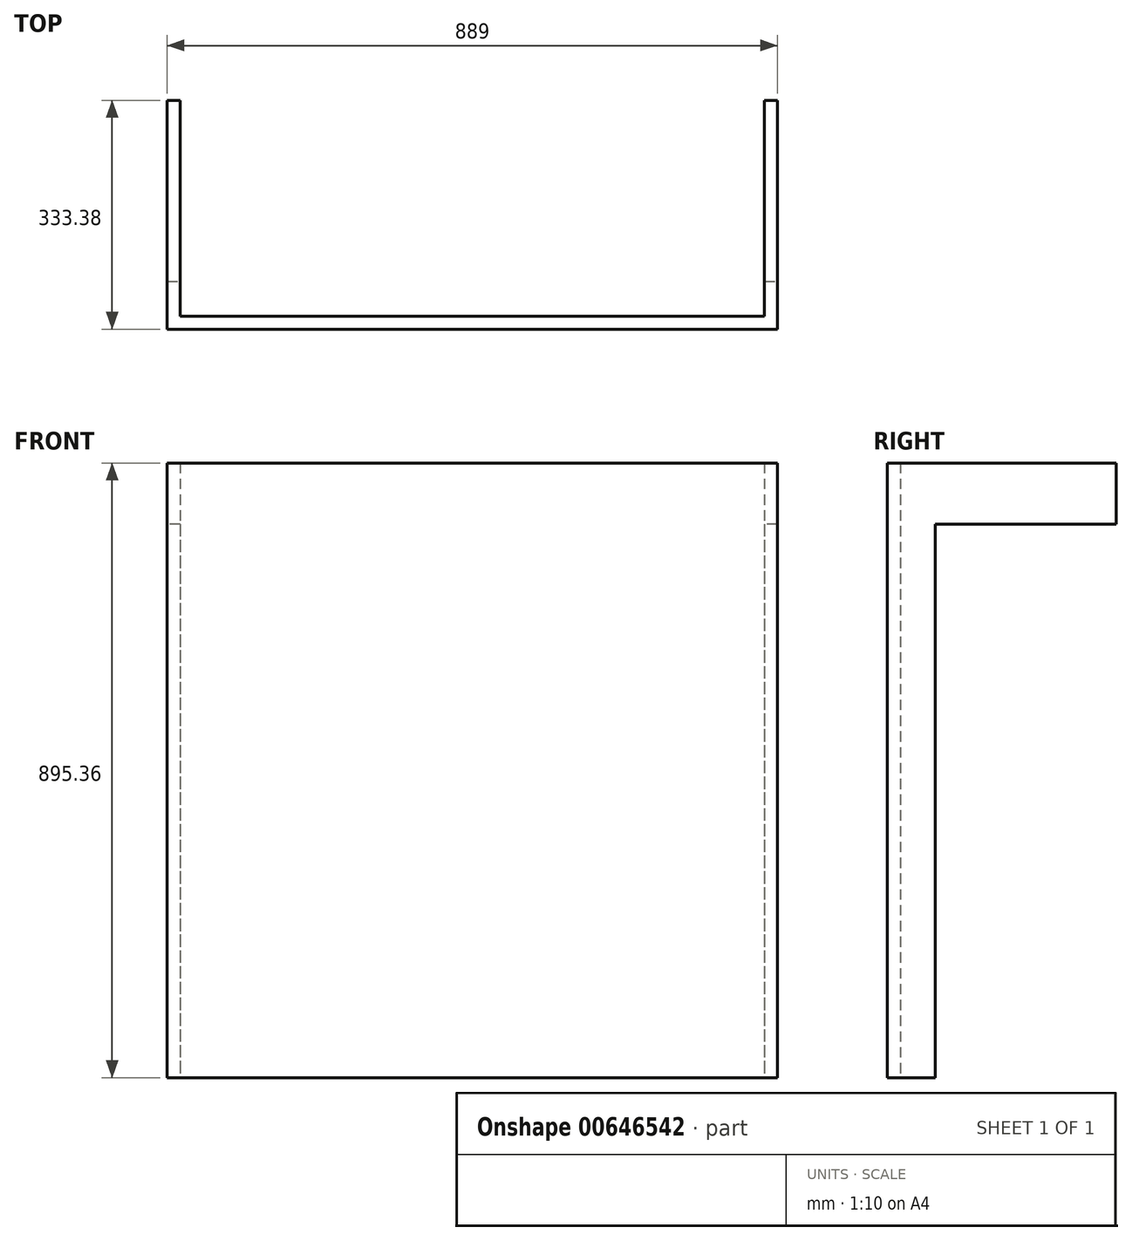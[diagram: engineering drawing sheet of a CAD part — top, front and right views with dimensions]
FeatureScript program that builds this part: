
annotation { "Feature Type Name" : "Feature", "Feature Type Description" : "" }
export const myFeature = defineFeature(function(context is Context, id is Id, definition is map)
    precondition{}
    {
        {
            var Q0;
            Q0=qCreatedBy(makeId("Front.planeOp"),FACE);
            var sketch = newSketch(context, id + "F0", { "sketchPlane" : qUnion([Q0])});
            skLineSegment(sketch, "E0.bottom", {"start": v(-444.5, 447.68) * mm, "end": v(444.5, 447.68) * mm});
            skLineSegment(sketch, "E0.top", {"start": v(-444.5, -447.68) * mm, "end": v(444.5, -447.68) * mm});
            skLineSegment(sketch, "E0.left", {"start": v(-444.5, 447.68) * mm, "end": v(-444.5, -447.68) * mm});
            skLineSegment(sketch, "E0.right", {"start": v(444.5, 447.68) * mm, "end": v(444.5, -447.68) * mm});
            skPoint(sketch, "E0.middle", {"position": v(0, 0) * mm});
            skSolve(sketch);
        }
        {
            var Q0;
            Q0=makeQuery(id+"F0.imprint","IMPRINT",FACE,{"disambiguationData":[TD([[makeQuery(id+"F0.imprint","IMPRINT",EDGE,{"derivedFrom":sQuery(id+"F0.wireOp",EDGE,"E0.bottom")}),-1.0]])]});
            extrude(context, id + "F1", {"entities" : qUnion([Q0]), "depth" : 19.05 * mm, "offsetDistance" : 25.4 * mm});
        }
        {
            var Q0;
            Q0=makeQuery(id+"F1.opExtrude","CAP_FACE",FACE,{"disambiguationData":[OSD([sQuery(id+"F0.wireOp",EDGE,"E0.bottom"),sQuery(id+"F0.wireOp",EDGE,"E0.top"),sQuery(id+"F0.wireOp",EDGE,"E0.left"),sQuery(id+"F0.wireOp",EDGE,"E0.right")])],"isStart":true});
            var sketch = newSketch(context, id + "F2", { "sketchPlane" : qUnion([Q0])});
            skLineSegment(sketch, "E1.bottom", {"start": v(-444.5, 447.68) * mm, "end": v(-425.45, 447.68) * mm});
            skLineSegment(sketch, "E1.top", {"start": v(-444.5, -447.68) * mm, "end": v(-425.45, -447.68) * mm});
            skLineSegment(sketch, "E1.left", {"start": v(-444.5, 447.68) * mm, "end": v(-444.5, -447.68) * mm});
            skLineSegment(sketch, "E1.right", {"start": v(-425.45, 447.68) * mm, "end": v(-425.45, -447.68) * mm});
            skLineSegment(sketch, "E2.bottom", {"start": v(444.5, 447.68) * mm, "end": v(425.45, 447.68) * mm});
            skLineSegment(sketch, "E2.top", {"start": v(444.5, -447.68) * mm, "end": v(425.45, -447.68) * mm});
            skLineSegment(sketch, "E2.left", {"start": v(444.5, 447.68) * mm, "end": v(444.5, -447.68) * mm});
            skLineSegment(sketch, "E2.right", {"start": v(425.45, 447.68) * mm, "end": v(425.45, -447.68) * mm});
            skSolve(sketch);
        }
        {
            var Q0;
            Q0=makeQuery(id+"F2.imprint","IMPRINT",FACE,{"disambiguationData":[TD([[makeQuery(id+"F2.imprint","IMPRINT",EDGE,{"derivedFrom":sQuery(id+"F2.wireOp",EDGE,"E1.bottom")}),1.0]])]});
            var Q1;
            Q1=makeQuery(id+"F2.imprint","IMPRINT",FACE,{"disambiguationData":[TD([[makeQuery(id+"F2.imprint","IMPRINT",EDGE,{"derivedFrom":sQuery(id+"F2.wireOp",EDGE,"E2.bottom")}),1.0]])]});
            extrude(context, id + "F3", {"entities" : qUnion([Q0, Q1]), "operationType" : NewBodyOperationType.ADD, "depth" : 50.8 * mm, "offsetDistance" : 25.4 * mm});
        }
        {
            var Q0;
            Q0=makeQuery(id+"F3.opExtrude","CAP_FACE",FACE,{"disambiguationData":[OSD([sQuery(id+"F2.wireOp",EDGE,"E1.bottom"),sQuery(id+"F2.wireOp",EDGE,"E1.top"),sQuery(id+"F2.wireOp",EDGE,"E1.left"),sQuery(id+"F2.wireOp",EDGE,"E1.right")])],"isStart":false});
            var sketch = newSketch(context, id + "F4", { "sketchPlane" : qUnion([Q0])});
            skLineSegment(sketch, "E3.bottom", {"start": v(-444.5, 447.68) * mm, "end": v(-425.45, 447.68) * mm});
            skLineSegment(sketch, "E3.top", {"start": v(-444.5, 358.77) * mm, "end": v(-425.45, 358.77) * mm});
            skLineSegment(sketch, "E3.left", {"start": v(-444.5, 447.68) * mm, "end": v(-444.5, 358.77) * mm});
            skLineSegment(sketch, "E3.right", {"start": v(-425.45, 447.68) * mm, "end": v(-425.45, 358.77) * mm});
            skSolve(sketch);
        }
        {
            var Q0;
            Q0=makeQuery(id+"F4.imprint","IMPRINT",FACE,{"disambiguationData":[TD([[makeQuery(id+"F4.imprint","IMPRINT",EDGE,{"derivedFrom":sQuery(id+"F4.wireOp",EDGE,"E3.bottom")}),1.0]])]});
            extrude(context, id + "F5", {"entities" : qUnion([Q0]), "operationType" : NewBodyOperationType.ADD, "depth" : 263.52 * mm, "offsetDistance" : 25.4 * mm});
        }
        {
            var Q0;
            Q0=makeQuery(id+"F3.opExtrude","CAP_FACE",FACE,{"disambiguationData":[OSD([sQuery(id+"F2.wireOp",EDGE,"E2.bottom"),sQuery(id+"F2.wireOp",EDGE,"E2.top"),sQuery(id+"F2.wireOp",EDGE,"E2.left"),sQuery(id+"F2.wireOp",EDGE,"E2.right")])],"isStart":false});
            var sketch = newSketch(context, id + "F6", { "sketchPlane" : qUnion([Q0])});
            skLineSegment(sketch, "E4.bottom", {"start": v(425.45, 447.68) * mm, "end": v(444.5, 447.68) * mm});
            skLineSegment(sketch, "E4.top", {"start": v(425.45, 358.77) * mm, "end": v(444.5, 358.77) * mm});
            skLineSegment(sketch, "E4.left", {"start": v(425.45, 447.68) * mm, "end": v(425.45, 358.77) * mm});
            skLineSegment(sketch, "E4.right", {"start": v(444.5, 447.68) * mm, "end": v(444.5, 358.78) * mm});
            skSolve(sketch);
        }
        {
            var Q0;
            Q0=makeQuery(id+"F6.imprint","IMPRINT",FACE,{"disambiguationData":[TD([[makeQuery(id+"F6.imprint","IMPRINT",EDGE,{"derivedFrom":sQuery(id+"F6.wireOp",EDGE,"E4.bottom")}),1.0]])]});
            extrude(context, id + "F7", {"entities" : qUnion([Q0]), "operationType" : NewBodyOperationType.ADD, "depth" : 263.52 * mm, "offsetDistance" : 25.4 * mm});
        }
    });
